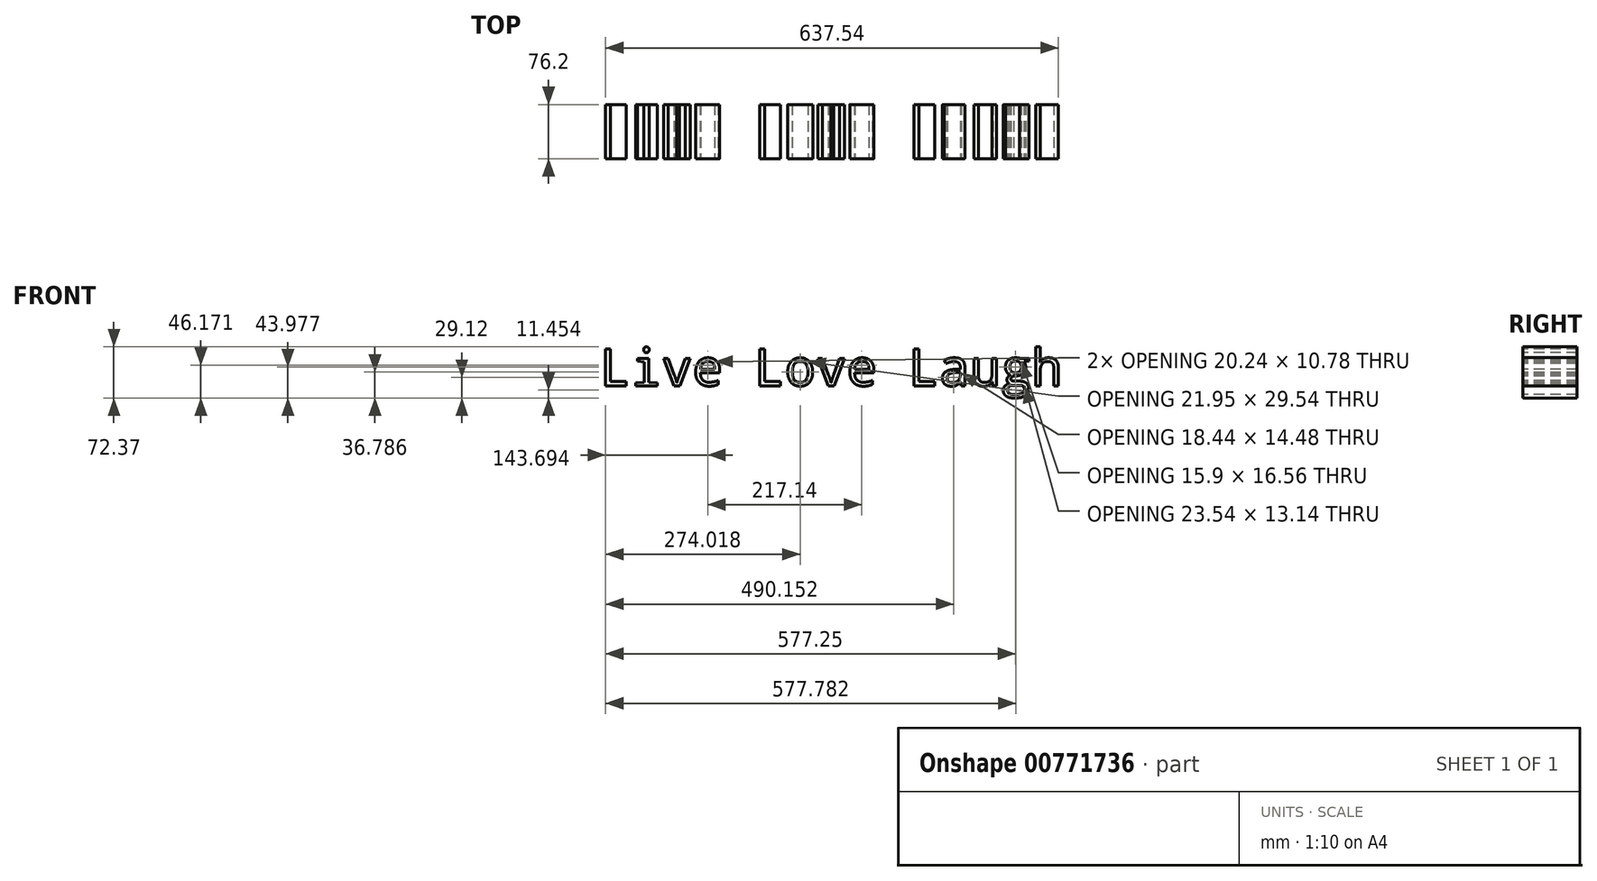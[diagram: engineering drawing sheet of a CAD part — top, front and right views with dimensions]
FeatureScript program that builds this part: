
annotation { "Feature Type Name" : "Feature", "Feature Type Description" : "" }
export const myFeature = defineFeature(function(context is Context, id is Id, definition is map)
    precondition{}
    {
        {
            var Q0;
            Q0=qCreatedBy(makeId("Front.planeOp"),FACE);
            var sketch = newSketch(context, id + "F0", { "sketchPlane" : qUnion([Q0])});
            skText(sketch, "E0", { "text": "Live Love Laugh", "fontName": "DroidSansMono.ttf"});
            const initialGuessF0  = {"E0": [-0.1192, -0.02338, 1, 0, 0.0521]};
            skSetInitialGuess(sketch, initialGuessF0);
            skSolve(sketch);
        }
        {
            var Q0;
            Q0=qSketchRegion(id+"F0",true);
            extrude(context, id + "F1", {"entities" : qUnion([Q0]), "oppositeDirection" : true, "depth" : 76.2 * mm, "offsetDistance" : 25.4 * mm});
        }
    });
